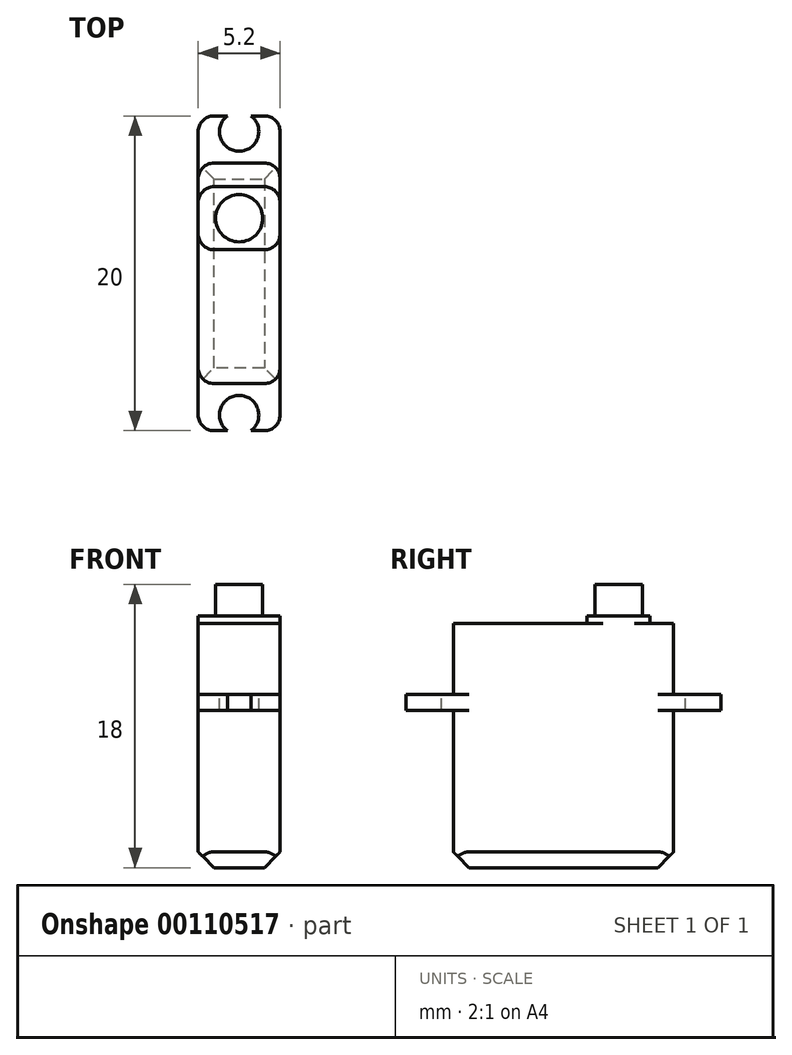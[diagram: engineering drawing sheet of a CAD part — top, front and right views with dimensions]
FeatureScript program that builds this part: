
annotation { "Feature Type Name" : "Feature", "Feature Type Description" : "" }
export const myFeature = defineFeature(function(context is Context, id is Id, definition is map)
    precondition{}
    {
        {
            var Q0;
            Q0=qCreatedBy(makeId("Right.planeOp"),FACE);
            var sketch = newSketch(context, id + "F0", { "sketchPlane" : qUnion([Q0])});
            skLineSegment(sketch, "E0", {"start": v(0, 10) * mm, "end": v(0, 0) * mm});
            skLineSegment(sketch, "E1", {"start": v(0, 0) * mm, "end": v(-14, 0) * mm});
            skLineSegment(sketch, "E2", {"start": v(-14, 0) * mm, "end": v(-14, 10) * mm});
            skLineSegment(sketch, "E3", {"start": v(-14, 10) * mm, "end": v(-17, 10) * mm});
            skLineSegment(sketch, "E4", {"start": v(-17, 10) * mm, "end": v(-17, 11) * mm});
            skLineSegment(sketch, "E5", {"start": v(3, 11) * mm, "end": v(3, 10) * mm});
            skLineSegment(sketch, "E6", {"start": v(3, 10) * mm, "end": v(0, 10) * mm});
            skLineSegment(sketch, "E7", {"start": v(-17, 11) * mm, "end": v(-14, 11) * mm});
            skLineSegment(sketch, "E8", {"start": v(-14, 11) * mm, "end": v(-14, 15.5) * mm});
            skLineSegment(sketch, "E9", {"start": v(-14, 15.5) * mm, "end": v(0, 15.5) * mm});
            skLineSegment(sketch, "E10", {"start": v(0, 15.5) * mm, "end": v(0, 11) * mm});
            skLineSegment(sketch, "E11", {"start": v(0, 11) * mm, "end": v(3, 11) * mm});
            skLineSegment(sketch, "E12", {"start": v(-5.5, 15.5) * mm, "end": v(-5.5, 16) * mm});
            skLineSegment(sketch, "E13", {"start": v(-5.5, 16) * mm, "end": v(-1.5, 16) * mm});
            skLineSegment(sketch, "E14", {"start": v(-1.5, 16) * mm, "end": v(-1.5, 15.5) * mm});
            skLineSegment(sketch, "E15", {"start": v(-3.5, 16) * mm, "end": v(-3.5, 0) * mm, "construction": true});
            skSolve(sketch);
        }
        {
            var Q0;
            Q0=qSketchRegion(id+"F0",true);
            extrude(context, id + "F1", {"entities" : qUnion([Q0]), "endBound" : BoundingType.SYMMETRIC, "depth" : 5.2 * mm});
        }
        {
            var Q0;
            Q0=makeQuery(id+"F1.opExtrude","SWEPT_FACE",FACE,{"disambiguationData":[OSD([sQuery(id+"F0.wireOp",EDGE,"E13")])]});
            var sketch = newSketch(context, id + "F2", { "sketchPlane" : qUnion([Q0])});
            skCircle(sketch, "E16", {"center": v(0, -3.5) * mm, "radius": 1.5 * mm});
            skPoint(sketch, "E16.centerSnap0", {"position": v(2.6, -3.5) * mm});
            skSolve(sketch);
        }
        {
            var Q0;
            Q0=qSketchRegion(id+"F2",true);
            extrude(context, id + "F3", {"entities" : qUnion([Q0]), "operationType" : NewBodyOperationType.ADD, "depth" : 2 * mm});
        }
        {
            var Q0;
            Q0=makeQuery(id+"F1.opExtrude","SWEPT_FACE",FACE,{"disambiguationData":[OSD([sQuery(id+"F0.wireOp",EDGE,"E1")])]});
            chamfer(context, id + "F4", {"entities" : qUnion([Q0]), "width" : 1 * mm, "tangentPropagation" : true});
        }
        {
            var Q0;
            Q0=makeQuery(id+"F1.opExtrude","CAP_EDGE",EDGE,{"disambiguationData":[OSD([sQuery(id+"F0.wireOp",EDGE,"E0")])],"isStart":false});
            var Q1;
            Q1=makeQuery(id+"F1.opExtrude","CAP_EDGE",EDGE,{"disambiguationData":[OSD([sQuery(id+"F0.wireOp",EDGE,"E10")])],"isStart":false});
            var Q2;
            Q2=makeQuery(id+"F1.opExtrude","CAP_EDGE",EDGE,{"disambiguationData":[OSD([sQuery(id+"F0.wireOp",EDGE,"E10")])],"isStart":true});
            var Q3;
            Q3=makeQuery(id+"F1.opExtrude","CAP_EDGE",EDGE,{"disambiguationData":[OSD([sQuery(id+"F0.wireOp",EDGE,"E14")])],"isStart":false});
            var Q4;
            Q4=makeQuery(id+"F1.opExtrude","CAP_EDGE",EDGE,{"disambiguationData":[OSD([sQuery(id+"F0.wireOp",EDGE,"E12")])],"isStart":false});
            var Q5;
            Q5=makeQuery(id+"F1.opExtrude","CAP_EDGE",EDGE,{"disambiguationData":[OSD([sQuery(id+"F0.wireOp",EDGE,"E12")])],"isStart":true});
            var Q6;
            Q6=makeQuery(id+"F1.opExtrude","CAP_EDGE",EDGE,{"disambiguationData":[OSD([sQuery(id+"F0.wireOp",EDGE,"E14")])],"isStart":true});
            var Q7;
            Q7=makeQuery(id+"F1.opExtrude","CAP_EDGE",EDGE,{"disambiguationData":[OSD([sQuery(id+"F0.wireOp",EDGE,"E8")])],"isStart":false});
            var Q8;
            Q8=makeQuery(id+"F1.opExtrude","CAP_EDGE",EDGE,{"disambiguationData":[OSD([sQuery(id+"F0.wireOp",EDGE,"E8")])],"isStart":true});
            var Q9;
            Q9=makeQuery(id+"F1.opExtrude","CAP_EDGE",EDGE,{"disambiguationData":[OSD([sQuery(id+"F0.wireOp",EDGE,"E4")])],"isStart":false});
            var Q10;
            Q10=makeQuery(id+"F1.opExtrude","CAP_EDGE",EDGE,{"disambiguationData":[OSD([sQuery(id+"F0.wireOp",EDGE,"E4")])],"isStart":true});
            var Q11;
            Q11=makeQuery(id+"F1.opExtrude","CAP_EDGE",EDGE,{"disambiguationData":[OSD([sQuery(id+"F0.wireOp",EDGE,"E2")])],"isStart":false});
            var Q12;
            Q12=makeQuery(id+"F1.opExtrude","CAP_EDGE",EDGE,{"disambiguationData":[OSD([sQuery(id+"F0.wireOp",EDGE,"E2")])],"isStart":true});
            var Q13;
            Q13=makeQuery(id+"F1.opExtrude","CAP_EDGE",EDGE,{"disambiguationData":[OSD([sQuery(id+"F0.wireOp",EDGE,"E5")])],"isStart":false});
            var Q14;
            Q14=makeQuery(id+"F1.opExtrude","CAP_EDGE",EDGE,{"disambiguationData":[OSD([sQuery(id+"F0.wireOp",EDGE,"E5")])],"isStart":true});
            var Q15;
            Q15=makeQuery(id+"F1.opExtrude","CAP_EDGE",EDGE,{"disambiguationData":[OSD([sQuery(id+"F0.wireOp",EDGE,"E0")])],"isStart":true});
            fillet(context, id + "F5", {"entities" : qUnion([Q0, Q1, Q2, Q3, Q4, Q5, Q6, Q7, Q8, Q9, Q10, Q11, Q12, Q13, Q14, Q15]), "radius" : 1 * mm, "tangentPropagation" : true, "allowEdgeOverflow" : false});
        }
        {
            var Q0;
            Q0=makeQuery(id+"F1.opExtrude","SWEPT_FACE",FACE,{"disambiguationData":[OSD([sQuery(id+"F0.wireOp",EDGE,"E11")])]});
            var sketch = newSketch(context, id + "F6", { "sketchPlane" : qUnion([Q0])});
            skCircle(sketch, "E17", {"center": v(0, 2) * mm, "radius": 1.25 * mm});
            skCircle(sketch, "E18", {"center": v(0, -16) * mm, "radius": 1.25 * mm});
            skSolve(sketch);
        }
        {
            var Q0;
            Q0=qSketchRegion(id+"F6",true);
            extrude(context, id + "F7", {"entities" : qUnion([Q0]), "operationType" : NewBodyOperationType.REMOVE, "oppositeDirection" : true, "depth" : 25 * mm});
        }
    });
